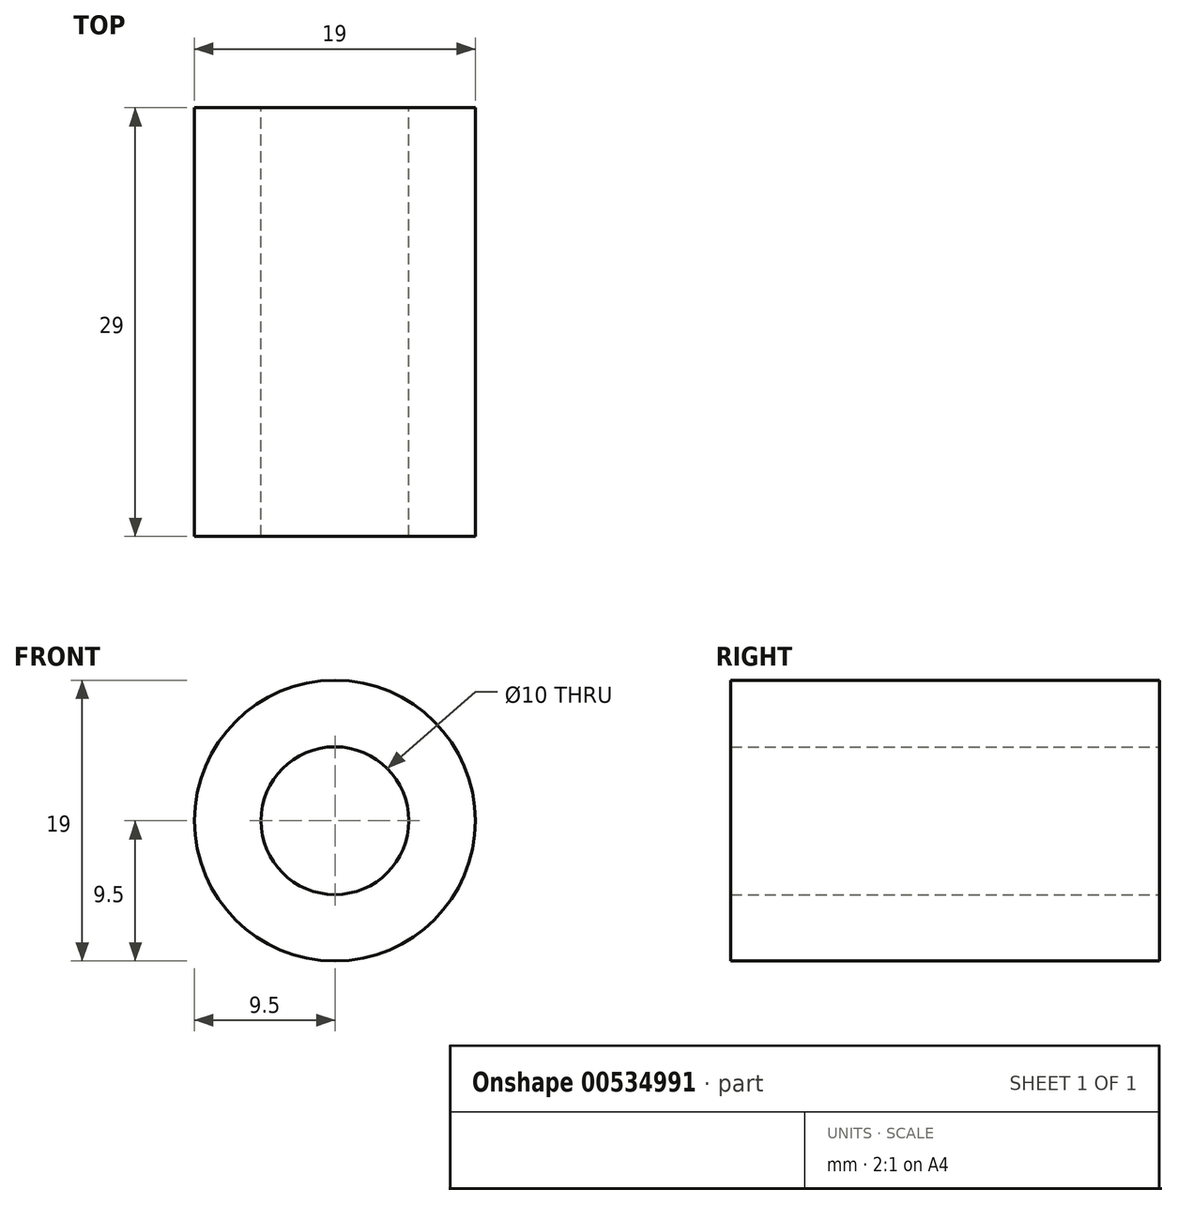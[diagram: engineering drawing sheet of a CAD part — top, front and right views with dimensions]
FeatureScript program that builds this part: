
annotation { "Feature Type Name" : "Feature", "Feature Type Description" : "" }
export const myFeature = defineFeature(function(context is Context, id is Id, definition is map)
    precondition{}
    {
        {
            var Q0;
            Q0=qCreatedBy(makeId("Front.planeOp"),FACE);
            var sketch = newSketch(context, id + "F0", { "sketchPlane" : qUnion([Q0])});
            skCircle(sketch, "E0", {"center": v(0, 0) * mm, "radius": 5 * mm});
            skCircle(sketch, "E1", {"center": v(0, 0) * mm, "radius": 9.5 * mm});
            skSolve(sketch);
        }
        {
            var Q0;
            Q0=makeQuery(id+"F0.imprint","IMPRINT",FACE,{"disambiguationData":[TD([[makeQuery(id+"F0.imprint","IMPRINT",EDGE,{"derivedFrom":sQuery(id+"F0.wireOp",EDGE,"E0")}),-1.0]])]});
            extrude(context, id + "F1", {"entities" : qUnion([Q0]), "depth" : 29 * mm, "offsetDistance" : 25 * mm});
        }
    });
